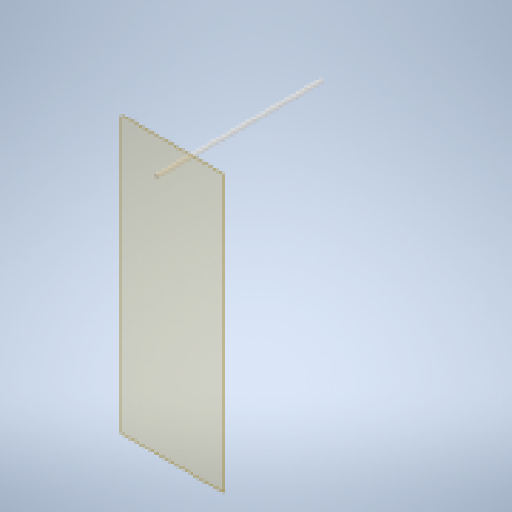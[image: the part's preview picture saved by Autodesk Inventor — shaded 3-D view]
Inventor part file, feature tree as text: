
AUTODESK INVENTOR PART (.ipt)
format: ipt  version: 2024.2 (Build 282272000, 272)  size: 116,736 bytes
history: native  units: mm
features: other x5, extrude x1, sketch x1, reference x1
ambient origin geometry x8: Origin, YZ Plane, XZ Plane, XY Plane, X Axis, Y Axis, Z Axis, Center Point
bodies: Body1 (feature_tree)
feature tree (8):
  other  "Твердое тело1"
  other  "РабПлоскость1"
  extrude  "Выдавливание1"  Depth=4.0mm
  sketch  "Эскиз1"
  reference  "Ссылка1"
  other  "<userpath>\Documents\Artist-v2\3D\Робот.iam"
  other  "Робот.iam"
  other  "бок:2"
